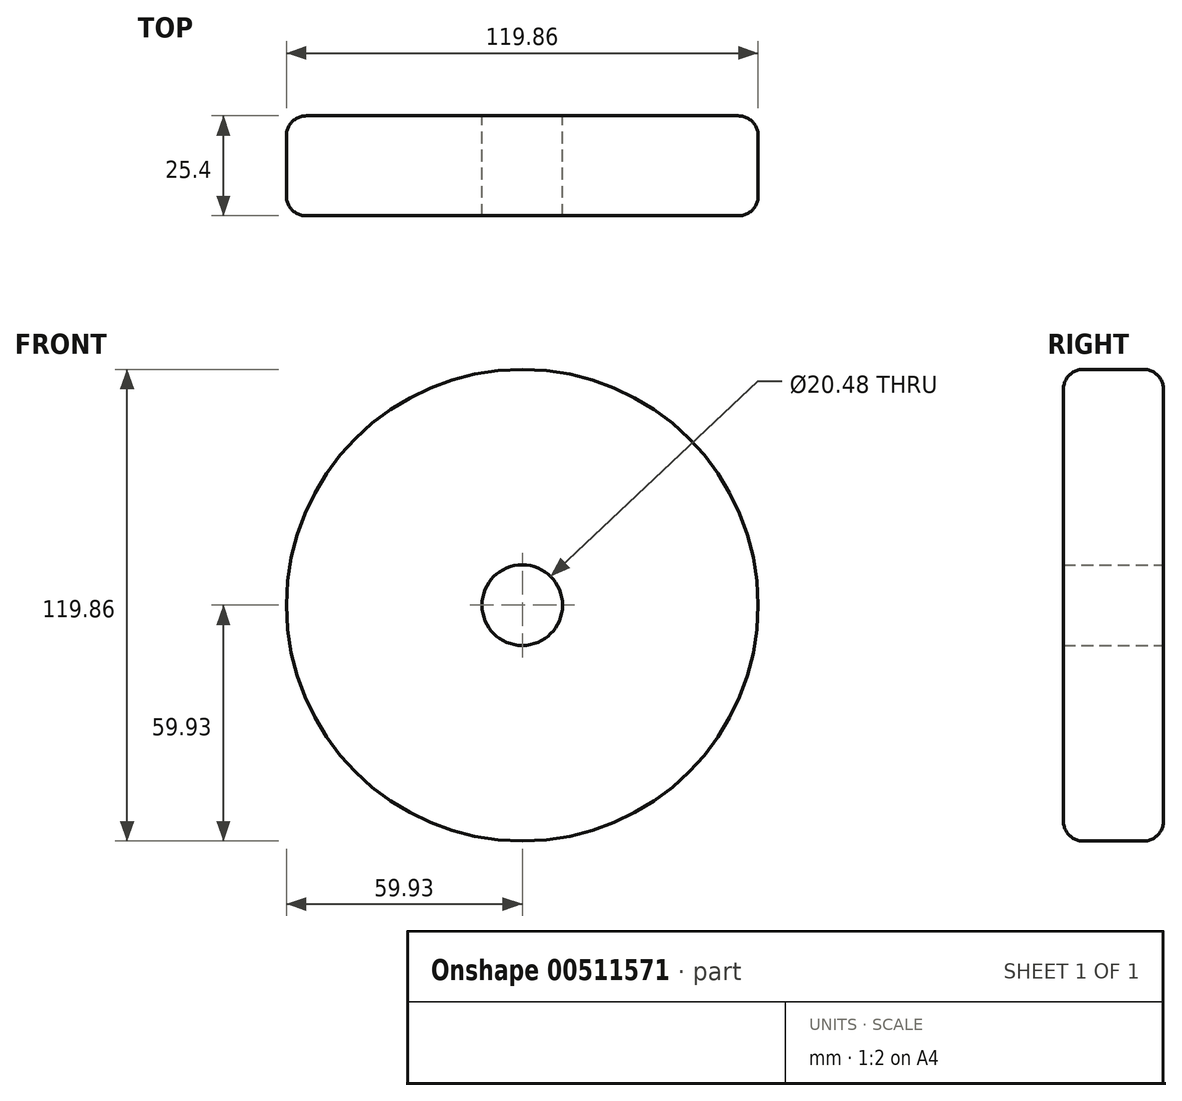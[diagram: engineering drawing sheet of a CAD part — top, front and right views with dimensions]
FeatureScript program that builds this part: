
annotation { "Feature Type Name" : "Feature", "Feature Type Description" : "" }
export const myFeature = defineFeature(function(context is Context, id is Id, definition is map)
    precondition{}
    {
        {
            var Q0;
            Q0=qCreatedBy(makeId("Front.planeOp"),FACE);
            var sketch = newSketch(context, id + "F0", { "sketchPlane" : qUnion([Q0])});
            skCircle(sketch, "E0", {"center": v(0, 0) * mm, "radius": 59.93 * mm});
            skCircle(sketch, "E1", {"center": v(0, 0) * mm, "radius": 10.24 * mm});
            skSolve(sketch);
        }
        {
            var Q0;
            Q0 = qSketchRegion(id + "F0", true);
            extrude(context, id + "F1", {"entities" : qUnion([Q0]), "depth" : 25.4 * mm, "offsetDistance" : 25.4 * mm});
        }
        {
            var Q0;
            Q0=makeQuery(id+"F1.opExtrude","SWEPT_FACE",FACE,{"disambiguationData":[OSD([sQuery(id+"F0.wireOp",EDGE,"E0")])]});
            fillet(context, id + "F2", {"entities" : qUnion([Q0]), "radius" : 5.08 * mm, "tangentPropagation" : true, "allowEdgeOverflow" : false});
        }
    });
